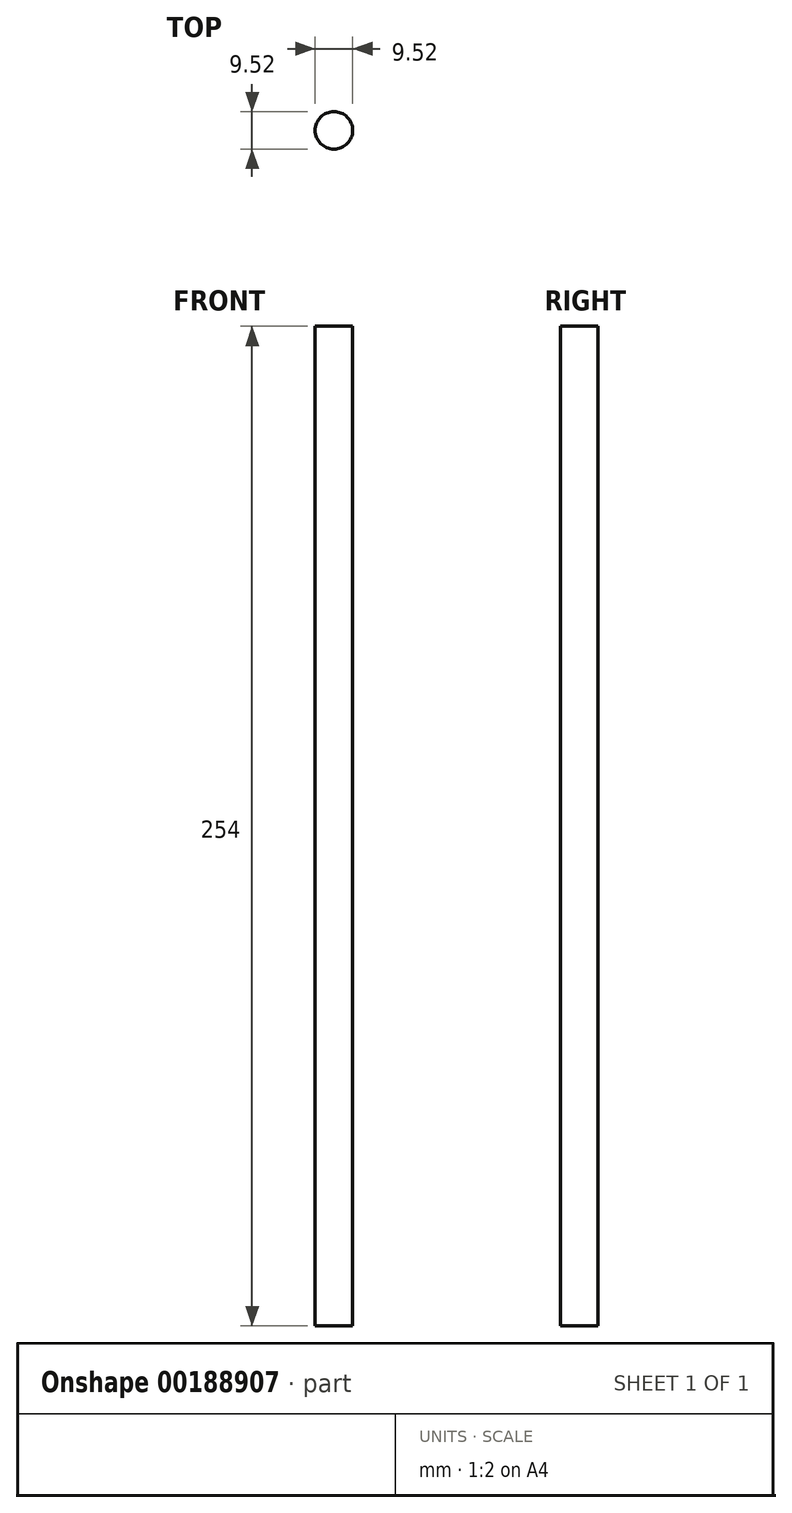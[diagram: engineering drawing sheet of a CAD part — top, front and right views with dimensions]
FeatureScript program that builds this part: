
annotation { "Feature Type Name" : "Feature", "Feature Type Description" : "" }
export const myFeature = defineFeature(function(context is Context, id is Id, definition is map)
    precondition{}
    {
        {
            var Q0;
            Q0=qCreatedBy(makeId("Top.planeOp"),FACE);
            var sketch = newSketch(context, id + "F0", { "sketchPlane" : qUnion([Q0])});
            skCircle(sketch, "E0", {"center": v(0, 0) * mm, "radius": 4.76 * mm});
            skSolve(sketch);
        }
        {
            var Q0;
            Q0=qSketchRegion(id+"F0",true);
            extrude(context, id + "F1", {"entities" : qUnion([Q0]), "depth" : 254 * mm});
        }
    });
